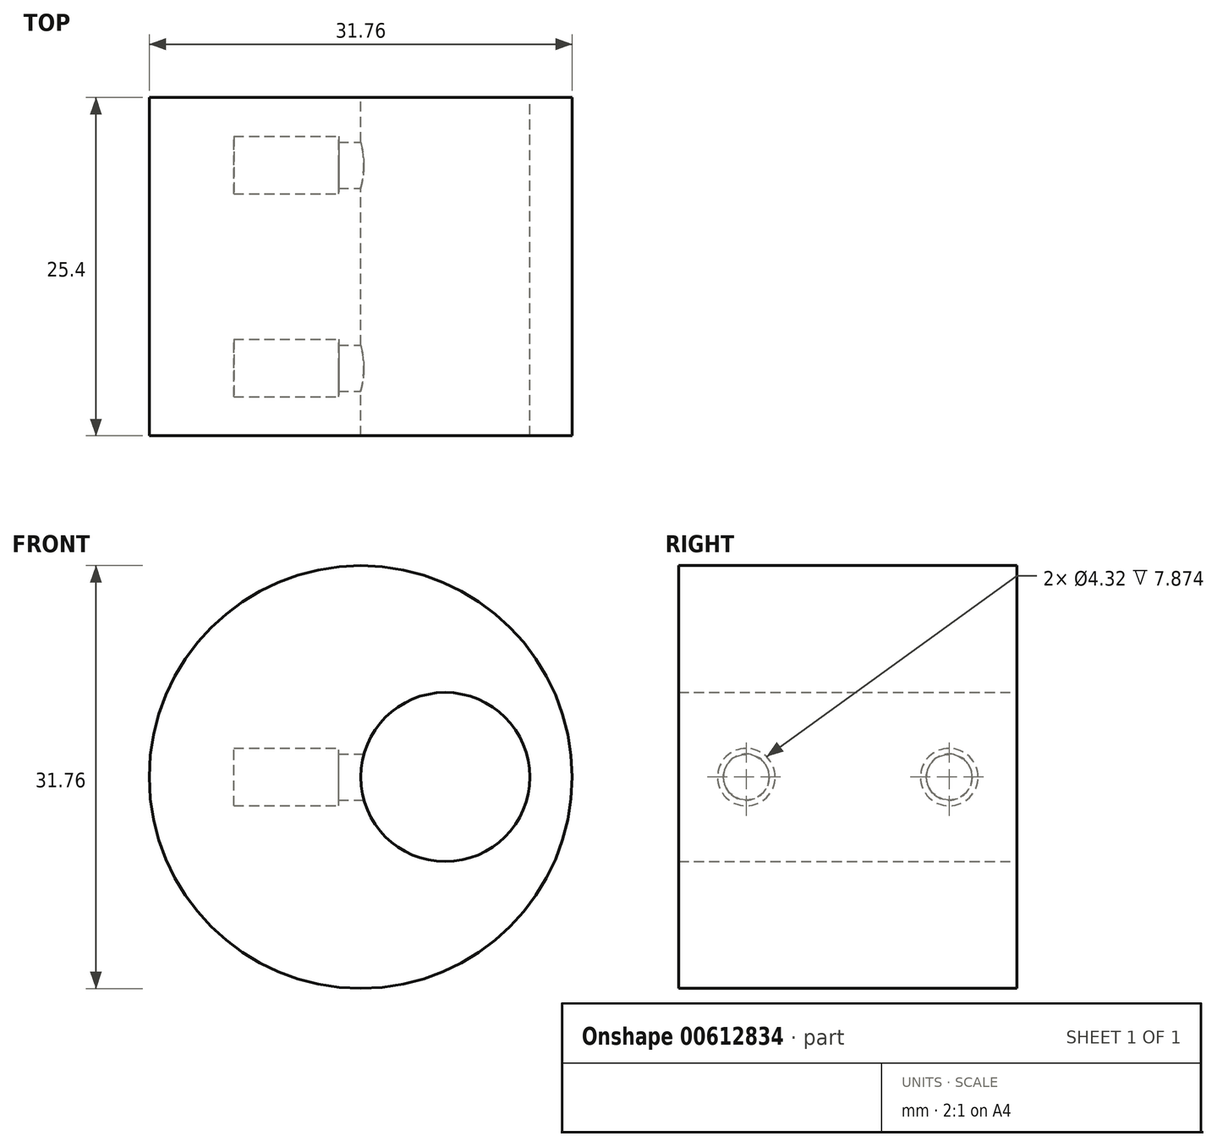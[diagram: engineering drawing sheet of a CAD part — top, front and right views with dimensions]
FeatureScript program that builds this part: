
annotation { "Feature Type Name" : "Feature", "Feature Type Description" : "" }
export const myFeature = defineFeature(function(context is Context, id is Id, definition is map)
    precondition{}
    {
        {
            var Q0;
            Q0=qCreatedBy(makeId("Front.planeOp"),FACE);
            var sketch = newSketch(context, id + "F0", { "sketchPlane" : qUnion([Q0])});
            skCircle(sketch, "E0", {"center": v(-6.35, 0) * mm, "radius": 15.88 * mm});
            skCircle(sketch, "E1", {"center": v(0, 0) * mm, "radius": 6.35 * mm});
            skSolve(sketch);
        }
        {
            var Q0;
            Q0=qSketchRegion(id+"F0",true);
            extrude(context, id + "F1", {"entities" : qUnion([Q0]), "depth" : 25.4 * mm, "symmetric" : true});
        }
        {
            var Q0;
            Q0=qCreatedBy(makeId("Right.planeOp"),FACE);
            cPlane(context, id + "F2", {"entities" : qUnion([Q0]), "cplaneType" : CPlaneType.OFFSET, "offset" : 15.88 * mm, "oppositeDirection" : true, "width" : 152.4 * mm, "height" : 152.4 * mm});
        }
        {
            var Q0;
            Q0=qCreatedBy(id+"F2.planeOp",FACE);
            var sketch = newSketch(context, id + "F3", { "sketchPlane" : qUnion([Q0])});
            skPoint(sketch, "E2", {"position": v(7.62, 0) * mm});
            skPoint(sketch, "E3", {"position": v(-7.62, 0) * mm});
            skSolve(sketch);
        }
        {
            var Q0;
            Q0=sQuery(id+"F3.wireOp",VERTEX,"E2");
            var Q1;
            Q1=sQuery(id+"F3.wireOp",VERTEX,"E3");
            var Q2;
            Q2=makeQuery(id+"F1.opExtrude","SWEPT_BODY",BODY,{"disambiguationData":[OSD([sQuery(id+"F0.wireOp",EDGE,"E0"),sQuery(id+"F0.wireOp",EDGE,"E1")])]});
            hole(context, id + "F4", {"style" : HoleStyle.C_BORE, "holeDiameter" : 3.45 * mm, "cBoreDiameter" : 4.32 * mm, "cBoreDepth" : 7.87 * mm, "endStyle" : HoleEndStyle.BLIND, "oppositeDirection" : true, "holeDepth" : 19.05 * mm, "locations" : qUnion([Q0, Q1]), "scope" : qUnion([Q2])});
        }
    });
